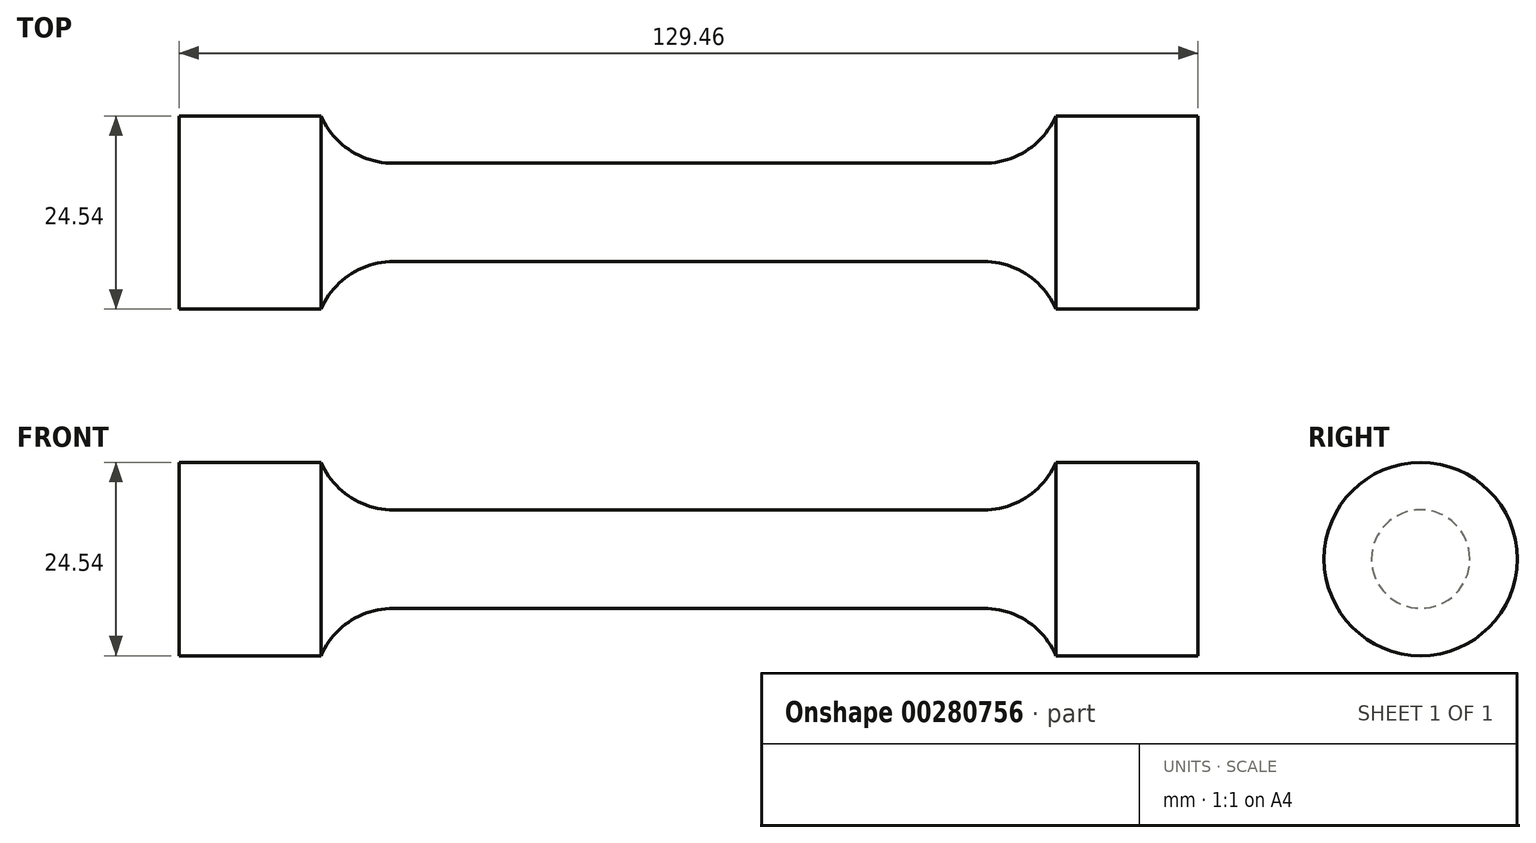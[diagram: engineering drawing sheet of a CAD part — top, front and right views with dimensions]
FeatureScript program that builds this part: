
annotation { "Feature Type Name" : "Feature", "Feature Type Description" : "" }
export const myFeature = defineFeature(function(context is Context, id is Id, definition is map)
    precondition{}
    {
        {
            var Q0;
            Q0=qCreatedBy(makeId("Front.planeOp"),FACE);
            var sketch = newSketch(context, id + "F0", { "sketchPlane" : qUnion([Q0])});
            skLineSegment(sketch, "E0", {"start": v(0, 6.25) * mm, "end": v(37.5, 6.25) * mm});
            skArc(sketch, "E1", {"start": v(37.5, 6.25) * mm, "mid": v(42.99, 7.89) * mm, "end": v(46.67, 12.27) * mm});
            skLineSegment(sketch, "E2", {"start": v(46.67, 12.27) * mm, "end": v(64.73, 12.27) * mm});
            skLineSegment(sketch, "E3", {"start": v(64.73, 12.27) * mm, "end": v(64.73, 0) * mm});
            skLineSegment(sketch, "E4.MirrorCS", {"start": v(0, 6.25) * mm, "end": v(-37.5, 6.25) * mm});
            skLineSegment(sketch, "E5.MirrorCS", {"start": v(-64.73, 12.27) * mm, "end": v(-64.73, 0) * mm});
            skLineSegment(sketch, "E6.MirrorCS", {"start": v(-46.67, 12.27) * mm, "end": v(-64.73, 12.27) * mm});
            skArc(sketch, "E7.MirrorCS", {"start": v(-37.5, 6.25) * mm, "mid": v(-42.99, 7.89) * mm, "end": v(-46.67, 12.27) * mm});
            skLineSegment(sketch, "E8", {"start": v(-64.73, 0) * mm, "end": v(64.73, 0) * mm});
            skSolve(sketch);
        }
        {
            var Q0;
            Q0=makeQuery(id+"F0.imprint","IMPRINT",FACE,{"disambiguationData":[TD([[makeQuery(id+"F0.imprint","IMPRINT",EDGE,{"derivedFrom":sQuery(id+"F0.wireOp",EDGE,"E0")}),-1.0]])]});
            var Q1;
            Q1=sQuery(id+"F0.wireOp",EDGE,"E8");
            revolve(context, id + "F1", {"entities" : qUnion([Q0]), "axis" : qUnion([Q1]), "revolveType" : RevolveType.FULL});
        }
    });
